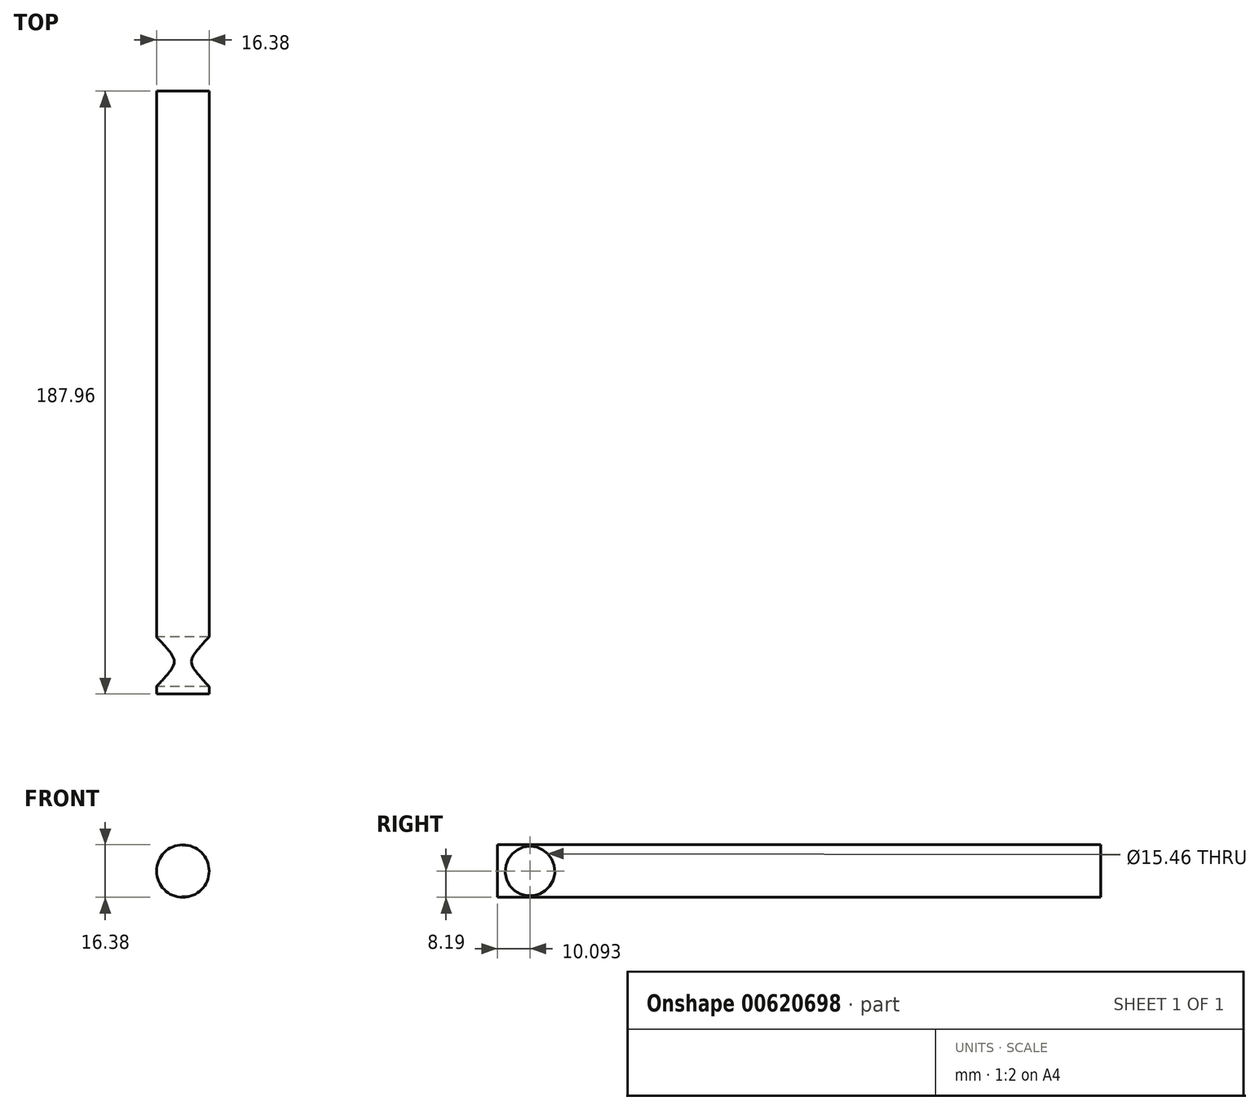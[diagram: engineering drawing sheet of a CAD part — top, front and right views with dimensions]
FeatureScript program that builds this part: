
annotation { "Feature Type Name" : "Feature", "Feature Type Description" : "" }
export const myFeature = defineFeature(function(context is Context, id is Id, definition is map)
    precondition{}
    {
        {
            var Q0;
            Q0=qCreatedBy(makeId("Front.planeOp"),FACE);
            var sketch = newSketch(context, id + "F0", { "sketchPlane" : qUnion([Q0])});
            skCircle(sketch, "E0", {"center": v(0, 0) * mm, "radius": 8.19 * mm});
            skSolve(sketch);
        }
        {
            var Q0;
            Q0=makeQuery(id+"F0.imprint","IMPRINT",FACE,{"disambiguationData":[TD([[makeQuery(id+"F0.imprint","IMPRINT",EDGE,{"derivedFrom":sQuery(id+"F0.wireOp",EDGE,"E0")}),1.0]])]});
            extrude(context, id + "F1", {"entities" : qUnion([Q0]), "depth" : 187.96 * mm, "offsetDistance" : 25.4 * mm, "symmetric" : true});
        }
        {
            var Q0;
            Q0=qCreatedBy(makeId("Right.planeOp"),FACE);
            var sketch = newSketch(context, id + "F2", { "sketchPlane" : qUnion([Q0])});
            skCircle(sketch, "E1", {"center": v(-83.89, 0) * mm, "radius": 7.73 * mm});
            skSolve(sketch);
        }
        {
            var Q0;
            Q0 = qSketchRegion(id + "F2", true);
            extrude(context, id + "F3", {"entities" : qUnion([Q0]), "operationType" : NewBodyOperationType.REMOVE, "depth" : 25.4 * mm, "offsetDistance" : 25.4 * mm, "symmetric" : true});
        }
    });
